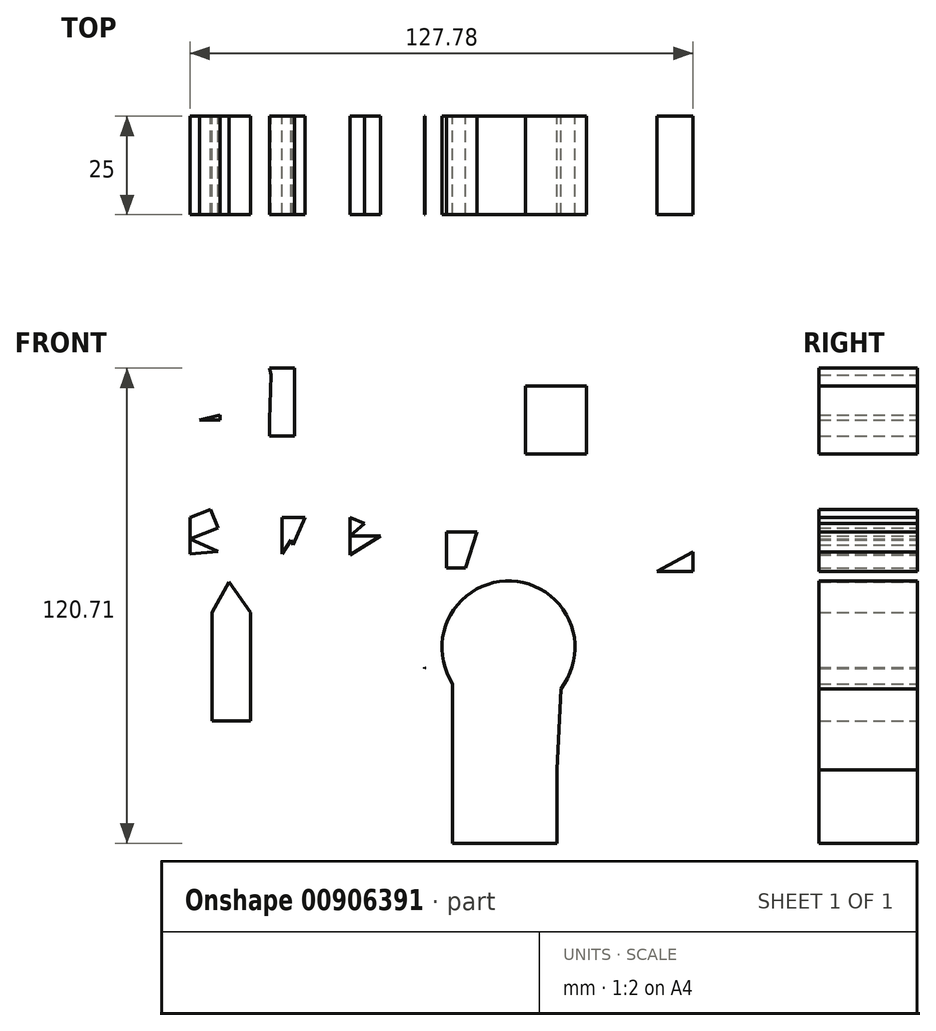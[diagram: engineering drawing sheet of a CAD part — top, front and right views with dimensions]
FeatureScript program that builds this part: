
annotation { "Feature Type Name" : "Feature", "Feature Type Description" : "" }
export const myFeature = defineFeature(function(context is Context, id is Id, definition is map)
    precondition{}
    {
        {
            var Q0;
            Q0=qCreatedBy(makeId("Front.planeOp"),FACE);
            var sketch = newSketch(context, id + "F0", { "sketchPlane" : qUnion([Q0])});
            skArc(sketch, "E0.cCircle", {"start": v(18.84, 36.8) * mm, "mid": v(19.66, -22.39) * mm, "end": v(22.97, 36.71) * mm, "construction": true});
            skLineSegment(sketch, "E0.0", {"start": v(-6.12, 20.79) * mm, "end": v(-3.98, 24.33) * mm});
            skLineSegment(sketch, "E0.1", {"start": v(-3.98, 24.33) * mm, "end": v(-1.36, 27.54) * mm});
            skLineSegment(sketch, "E0.2", {"start": v(-1.36, 27.54) * mm, "end": v(1.68, 30.35) * mm});
            skLineSegment(sketch, "E0.3", {"start": v(1.68, 30.35) * mm, "end": v(5.08, 32.72) * mm});
            skLineSegment(sketch, "E0.4", {"start": v(5.08, 32.72) * mm, "end": v(8.78, 34.59) * mm});
            skLineSegment(sketch, "E0.5", {"start": v(8.78, 34.59) * mm, "end": v(12.7, 35.92) * mm});
            skLineSegment(sketch, "E0.6", {"start": v(12.7, 35.92) * mm, "end": v(16.77, 36.7) * mm});
            skLineSegment(sketch, "E0.7", {"start": v(16.77, 36.7) * mm, "end": v(18.84, 36.8) * mm});
            skLineSegment(sketch, "E0.8", {"start": v(22.97, 36.71) * mm, "end": v(25.03, 36.52) * mm});
            skLineSegment(sketch, "E0.9", {"start": v(25.03, 36.52) * mm, "end": v(29.06, 35.58) * mm});
            skLineSegment(sketch, "E0.10", {"start": v(29.06, 35.58) * mm, "end": v(32.92, 34.08) * mm});
            skLineSegment(sketch, "E0.11", {"start": v(32.92, 34.08) * mm, "end": v(36.54, 32.06) * mm});
            skLineSegment(sketch, "E0.12", {"start": v(36.54, 32.06) * mm, "end": v(39.84, 29.56) * mm});
            skLineSegment(sketch, "E0.13", {"start": v(39.84, 29.56) * mm, "end": v(42.75, 26.62) * mm});
            skLineSegment(sketch, "E0.14", {"start": v(42.75, 26.62) * mm, "end": v(45.24, 23.3) * mm});
            skLineSegment(sketch, "E0.15", {"start": v(45.24, 23.3) * mm, "end": v(47.23, 19.67) * mm});
            skLineSegment(sketch, "E0.16", {"start": v(47.23, 19.67) * mm, "end": v(48.7, 15.8) * mm});
            skLineSegment(sketch, "E0.17", {"start": v(48.7, 15.8) * mm, "end": v(49.62, 11.76) * mm});
            skLineSegment(sketch, "E0.18", {"start": v(49.62, 11.76) * mm, "end": v(49.97, 7.63) * mm});
            skLineSegment(sketch, "E0.19", {"start": v(49.97, 7.63) * mm, "end": v(49.73, 3.5) * mm});
            skLineSegment(sketch, "E0.20", {"start": v(49.73, 3.5) * mm, "end": v(48.93, -0.56) * mm});
            skLineSegment(sketch, "E0.21", {"start": v(48.93, -0.56) * mm, "end": v(47.57, -4.48) * mm});
            skLineSegment(sketch, "E0.22", {"start": v(47.57, -4.48) * mm, "end": v(45.67, -8.16) * mm});
            skLineSegment(sketch, "E0.23", {"start": v(45.67, -8.16) * mm, "end": v(43.29, -11.54) * mm});
            skLineSegment(sketch, "E0.24", {"start": v(43.29, -11.54) * mm, "end": v(40.45, -14.56) * mm});
            skLineSegment(sketch, "E0.25", {"start": v(40.45, -14.56) * mm, "end": v(37.22, -17.16) * mm});
            skLineSegment(sketch, "E0.26", {"start": v(37.22, -17.16) * mm, "end": v(33.67, -19.28) * mm});
            skLineSegment(sketch, "E0.27", {"start": v(33.67, -19.28) * mm, "end": v(29.85, -20.88) * mm});
            skLineSegment(sketch, "E0.28", {"start": v(29.85, -20.88) * mm, "end": v(25.84, -21.94) * mm});
            skLineSegment(sketch, "E0.29", {"start": v(25.84, -21.94) * mm, "end": v(21.73, -22.43) * mm});
            skLineSegment(sketch, "E0.30", {"start": v(21.73, -22.43) * mm, "end": v(17.6, -22.35) * mm});
            skLineSegment(sketch, "E0.31", {"start": v(17.6, -22.35) * mm, "end": v(13.5, -21.68) * mm});
            skLineSegment(sketch, "E0.32", {"start": v(13.5, -21.68) * mm, "end": v(9.55, -20.46) * mm});
            skLineSegment(sketch, "E0.33", {"start": v(9.55, -20.46) * mm, "end": v(5.8, -18.7) * mm});
            skLineSegment(sketch, "E0.34", {"start": v(5.8, -18.7) * mm, "end": v(2.33, -16.43) * mm});
            skLineSegment(sketch, "E0.35", {"start": v(2.33, -16.43) * mm, "end": v(-0.78, -13.7) * mm});
            skLineSegment(sketch, "E0.36", {"start": v(-0.78, -13.7) * mm, "end": v(-3.49, -10.56) * mm});
            skLineSegment(sketch, "E0.37", {"start": v(-3.49, -10.56) * mm, "end": v(-5.73, -7.08) * mm});
            skLineSegment(sketch, "E0.38", {"start": v(-5.73, -7.08) * mm, "end": v(-7.47, -3.32) * mm});
            skLineSegment(sketch, "E0.39", {"start": v(-7.47, -3.32) * mm, "end": v(-8.67, 0.64) * mm});
            skLineSegment(sketch, "E0.40", {"start": v(-8.67, 0.64) * mm, "end": v(-9.3, 4.73) * mm});
            skLineSegment(sketch, "E0.41", {"start": v(-9.3, 4.73) * mm, "end": v(-9.36, 8.88) * mm});
            skLineSegment(sketch, "E0.42", {"start": v(-9.36, 8.88) * mm, "end": v(-8.84, 12.99) * mm});
            skLineSegment(sketch, "E0.43", {"start": v(-8.84, 12.99) * mm, "end": v(-7.75, 16.98) * mm});
            skLineSegment(sketch, "E0.44", {"start": v(-7.75, 16.98) * mm, "end": v(-6.12, 20.79) * mm});
            skPoint(sketch, "E0.0.midPoint", {"position": v(-5.05, 22.56) * mm});
            skLineSegment(sketch, "E1", {"start": v(2.33, -16.43) * mm, "end": v(2.33, -16.7) * mm});
            skLineSegment(sketch, "E2", {"start": v(2.33, -16.7) * mm, "end": v(2.58, -16.52) * mm});
            skLineSegment(sketch, "E3", {"start": v(25.44, 0) * mm, "end": v(11.35, 0) * mm});
            skLineSegment(sketch, "E4", {"start": v(7.9, 8.88) * mm, "end": v(7.9, 17.96) * mm});
            skLineSegment(sketch, "E5", {"start": v(7.9, 17.96) * mm, "end": v(15.66, 17.96) * mm});
            skLineSegment(sketch, "E6", {"start": v(15.66, 17.96) * mm, "end": v(12.79, 8.88) * mm});
            skLineSegment(sketch, "E7", {"start": v(12.79, 8.88) * mm, "end": v(7.9, 8.88) * mm});
            skLineSegment(sketch, "E8", {"start": v(28.3, 17.96) * mm, "end": v(28.3, 6.47) * mm});
            skLineSegment(sketch, "E9", {"start": v(28.88, 6.47) * mm, "end": v(39.23, 6.47) * mm});
            skLineSegment(sketch, "E10", {"start": v(39.23, 6.47) * mm, "end": v(39.23, 17.96) * mm});
            skLineSegment(sketch, "E11", {"start": v(38.66, 19.4) * mm, "end": v(28.3, 17.96) * mm});
            skLineSegment(sketch, "E12", {"start": v(9.55, -20.46) * mm, "end": v(9.55, -42.4) * mm});
            skLineSegment(sketch, "E13", {"start": v(9.55, -42.4) * mm, "end": v(36.07, -42.4) * mm});
            skLineSegment(sketch, "E14", {"start": v(36.07, -42.4) * mm, "end": v(37.22, -17.16) * mm});
            skLineSegment(sketch, "E15", {"start": v(36.65, -29.78) * mm, "end": v(47.53, -33.15) * mm});
            skLineSegment(sketch, "E16", {"start": v(9.55, -31.43) * mm, "end": v(-4.45, -42.4) * mm});
            skLineSegment(sketch, "E17", {"start": v(9.55, -42.4) * mm, "end": v(9.55, -61.07) * mm});
            skLineSegment(sketch, "E18", {"start": v(9.55, -61.07) * mm, "end": v(36.07, -61.07) * mm});
            skLineSegment(sketch, "E19", {"start": v(36.07, -61.07) * mm, "end": v(36.07, -42.4) * mm});
            skLineSegment(sketch, "E20", {"start": v(15.66, -61.07) * mm, "end": v(15.66, -77.46) * mm});
            skLineSegment(sketch, "E21", {"start": v(30.32, -61.07) * mm, "end": v(30.32, -77.74) * mm});
            skLineSegment(sketch, "E22", {"start": v(-6.12, 23.71) * mm, "end": v(-14.89, 24.11) * mm});
            skLineSegment(sketch, "E23", {"start": v(-9.34, 30.6) * mm, "end": v(-1.36, 27.54) * mm});
            skLineSegment(sketch, "E24", {"start": v(-1.36, 36.07) * mm, "end": v(1.68, 30.35) * mm});
            skLineSegment(sketch, "E25", {"start": v(9.55, 40.96) * mm, "end": v(12.7, 35.92) * mm});
            skLineSegment(sketch, "E26", {"start": v(1.68, 40.1) * mm, "end": v(8.78, 34.59) * mm});
            skLineSegment(sketch, "E27", {"start": v(15.66, 43.83) * mm, "end": v(16.77, 36.7) * mm});
            skLineSegment(sketch, "E28", {"start": v(32.33, 44.7) * mm, "end": v(25.03, 36.52) * mm});
            skLineSegment(sketch, "E29", {"start": v(36.07, 42.1) * mm, "end": v(29.06, 35.58) * mm});
            skLineSegment(sketch, "E30", {"start": v(45.24, 23.3) * mm, "end": v(54.67, 30.35) * mm});
            skLineSegment(sketch, "E31", {"start": v(42.75, 26.62) * mm, "end": v(47.23, 38.26) * mm});
            skLineSegment(sketch, "E32", {"start": v(47.23, 19.67) * mm, "end": v(58.6, 25.92) * mm});
            skPoint(sketch, "E33.end.orphan", {"position": v(39.8, 42.1) * mm});
            skPoint(sketch, "E33.start.orphan", {"position": v(39.8, 35.58) * mm});
            skLineSegment(sketch, "E34", {"start": v(39.8, 35.58) * mm, "end": v(36.54, 32.06) * mm});
            skPoint(sketch, "E35.orphan", {"position": v(81.48, -49.87) * mm});
            skLineSegment(sketch, "E36", {"start": v(15.1, -42.4) * mm, "end": v(22.8, -42.4) * mm});
            skPoint(sketch, "E37.start.orphan", {"position": v(58.49, -49.87) * mm});
            skLineSegment(sketch, "E38", {"start": v(-47.28, -30.03) * mm, "end": v(-47.28, -59.06) * mm});
            skLineSegment(sketch, "E39", {"start": v(-47.28, -30.03) * mm, "end": v(-51.59, -30.03) * mm});
            skLineSegment(sketch, "E40", {"start": v(-47.28, -30.03) * mm, "end": v(-41.82, -30.03) * mm});
            skLineSegment(sketch, "E41", {"start": v(-41.82, -30.03) * mm, "end": v(-41.82, -2.44) * mm});
            skLineSegment(sketch, "E42", {"start": v(-41.82, -2.44) * mm, "end": v(-51.59, -2.44) * mm});
            skLineSegment(sketch, "E43", {"start": v(-51.59, -2.44) * mm, "end": v(-51.59, -30.03) * mm});
            skLineSegment(sketch, "E44", {"start": v(-51.59, -2.44) * mm, "end": v(-47.28, 5.32) * mm});
            skLineSegment(sketch, "E45", {"start": v(-47.28, 5.32) * mm, "end": v(-41.82, -2.44) * mm});
            skLineSegment(sketch, "E46", {"start": v(-44.55, -30.03) * mm, "end": v(-41.82, -36.64) * mm});
            skPoint(sketch, "E47.start.orphan", {"position": v(12.79, -49.87) * mm});
            skPoint(sketch, "E48.end.orphan", {"position": v(15.66, -49.87) * mm});
            skPoint(sketch, "E49.start.orphan", {"position": v(20.84, -49.87) * mm});
            skPoint(sketch, "E50.end.orphan", {"position": v(29.17, -42.4) * mm});
            skLineSegment(sketch, "E51", {"start": v(-47.28, 57.05) * mm, "end": v(-54.75, 57.05) * mm});
            skLineSegment(sketch, "E52", {"start": v(-54.75, 57.05) * mm, "end": v(-54.75, 51.02) * mm});
            skLineSegment(sketch, "E53", {"start": v(-54.75, 51.02) * mm, "end": v(-49.58, 51.02) * mm});
            skLineSegment(sketch, "E54", {"start": v(-49.58, 51.02) * mm, "end": v(-49.58, 46.42) * mm});
            skLineSegment(sketch, "E55", {"start": v(-49.58, 46.42) * mm, "end": v(-54.75, 46.42) * mm});
            skLineSegment(sketch, "E56", {"start": v(-54.75, 46.42) * mm, "end": v(-49.58, 47.75) * mm});
            skLineSegment(sketch, "E57", {"start": v(-36.93, 51.02) * mm, "end": v(-36.93, 42.4) * mm});
            skLineSegment(sketch, "E58", {"start": v(-36.93, 42.4) * mm, "end": v(-30.6, 42.4) * mm});
            skLineSegment(sketch, "E59", {"start": v(-30.6, 42.4) * mm, "end": v(-30.6, 59.64) * mm});
            skLineSegment(sketch, "E60", {"start": v(-30.6, 59.64) * mm, "end": v(-36.93, 59.64) * mm});
            skLineSegment(sketch, "E61", {"start": v(-36.93, 59.64) * mm, "end": v(-36.64, 57.91) * mm});
            skLineSegment(sketch, "E62", {"start": v(-36.64, 57.91) * mm, "end": v(-36.93, 46.42) * mm});
            skLineSegment(sketch, "E63", {"start": v(-19.1, 45.97) * mm, "end": v(-19.1, 59.64) * mm});
            skLineSegment(sketch, "E64", {"start": v(4.17, 59.64) * mm, "end": v(4.17, 50.15) * mm});
            skLineSegment(sketch, "E65", {"start": v(4.17, 50.15) * mm, "end": v(9.34, 50.15) * mm});
            skLineSegment(sketch, "E66", {"start": v(9.34, 50.73) * mm, "end": v(9.34, 58.78) * mm});
            skLineSegment(sketch, "E67", {"start": v(16.53, 58.78) * mm, "end": v(16.53, 50.15) * mm});
            skLineSegment(sketch, "E68", {"start": v(15.95, 49.3) * mm, "end": v(23.14, 58.78) * mm});
            skLineSegment(sketch, "E69", {"start": v(23.14, 57.34) * mm, "end": v(23.14, 50.15) * mm});
            skLineSegment(sketch, "E70", {"start": v(35.5, 58.78) * mm, "end": v(31.76, 50.15) * mm});
            skLineSegment(sketch, "E71", {"start": v(35.5, 58.78) * mm, "end": v(38.94, 50.15) * mm});
            skLineSegment(sketch, "E72", {"start": v(35.5, 54.46) * mm, "end": v(31.76, 50.15) * mm});
            skPoint(sketch, "E72.startSnap0", {"position": v(37.22, 54.46) * mm});
            skLineSegment(sketch, "E73", {"start": v(-65.67, 21.7) * mm, "end": v(-69.32, 13.28) * mm});
            skLineSegment(sketch, "E74", {"start": v(-65.67, 21.7) * mm, "end": v(-62.34, 13.37) * mm});
            skLineSegment(sketch, "E75", {"start": v(-67.4, 16.81) * mm, "end": v(-62.34, 14.62) * mm});
            skLineSegment(sketch, "E76", {"start": v(-62.34, 14.62) * mm, "end": v(-57.19, 12.39) * mm});
            skLineSegment(sketch, "E77", {"start": v(-57.19, 12.39) * mm, "end": v(-57.19, 21.7) * mm});
            skLineSegment(sketch, "E78", {"start": v(-57.19, 21.7) * mm, "end": v(-52.01, 23.77) * mm});
            skLineSegment(sketch, "E79", {"start": v(-52.01, 23.77) * mm, "end": v(-50.11, 19.01) * mm});
            skLineSegment(sketch, "E80", {"start": v(-50.11, 19.01) * mm, "end": v(-57.19, 16.18) * mm});
            skLineSegment(sketch, "E81", {"start": v(-57.19, 16.18) * mm, "end": v(-50.11, 13.12) * mm});
            skLineSegment(sketch, "E82", {"start": v(-50.11, 13.12) * mm, "end": v(-57.19, 12.39) * mm});
            skLineSegment(sketch, "E83", {"start": v(-40.1, 21.7) * mm, "end": v(-40.1, 12.39) * mm});
            skLineSegment(sketch, "E84", {"start": v(-33.77, 21.7) * mm, "end": v(-30.05, 12.39) * mm});
            skLineSegment(sketch, "E85", {"start": v(-32.05, 12.21) * mm, "end": v(-27.94, 21.7) * mm});
            skLineSegment(sketch, "E86", {"start": v(-27.94, 21.7) * mm, "end": v(-33.77, 12.39) * mm});
            skLineSegment(sketch, "E87", {"start": v(-33.77, 12.39) * mm, "end": v(-33.77, 21.7) * mm});
            skLineSegment(sketch, "E88", {"start": v(-33.77, 21.7) * mm, "end": v(-27.94, 21.7) * mm});
            skLineSegment(sketch, "E89", {"start": v(-27.94, 21.7) * mm, "end": v(-27.94, 12.21) * mm});
            skLineSegment(sketch, "E90", {"start": v(-24.57, 21.7) * mm, "end": v(-24.57, 12.21) * mm});
            skLineSegment(sketch, "E91", {"start": v(-24.57, 21.7) * mm, "end": v(-20.78, 12.21) * mm});
            skLineSegment(sketch, "E92", {"start": v(-20.84, 13.36) * mm, "end": v(-20.84, 23.77) * mm});
            skLineSegment(sketch, "E93", {"start": v(-16.53, 21.7) * mm, "end": v(-16.53, 12.21) * mm});
            skLineSegment(sketch, "E94", {"start": v(-16.53, 21.7) * mm, "end": v(-12.89, 20.12) * mm});
            skLineSegment(sketch, "E95", {"start": v(-12.89, 20.12) * mm, "end": v(-16.53, 16.96) * mm});
            skLineSegment(sketch, "E96", {"start": v(-16.53, 16.96) * mm, "end": v(-8.84, 16.98) * mm});
            skLineSegment(sketch, "E97", {"start": v(-8.84, 16.98) * mm, "end": v(-16.53, 12.21) * mm});
            skLineSegment(sketch, "E98", {"start": v(-16.24, 13.08) * mm, "end": v(-8.77, 12.94) * mm});
            skLineSegment(sketch, "E99", {"start": v(56.48, 11.76) * mm, "end": v(53.4, 4.67) * mm});
            skLineSegment(sketch, "E100", {"start": v(53.4, 4.67) * mm, "end": v(58.74, 16.98) * mm});
            skLineSegment(sketch, "E101", {"start": v(58.74, 16.98) * mm, "end": v(53.16, 19.4) * mm});
            skLineSegment(sketch, "E102", {"start": v(53.16, 19.4) * mm, "end": v(61.36, 16.98) * mm});
            skLineSegment(sketch, "E103", {"start": v(70.59, 12.99) * mm, "end": v(61.41, 7.94) * mm});
            skLineSegment(sketch, "E104", {"start": v(61.41, 7.94) * mm, "end": v(70.59, 7.94) * mm});
            skLineSegment(sketch, "E105", {"start": v(70.59, 7.94) * mm, "end": v(70.59, 12.99) * mm});
            skLineSegment(sketch, "E106.trimOffspring", {"start": v(28.3, 12.27) * mm, "end": v(39.23, 12.07) * mm});
            skLineSegment(sketch, "E107.trimOffspring", {"start": v(7.9, 12.64) * mm, "end": v(13.95, 12.53) * mm});
            skLineSegment(sketch, "E108.trimOffspring", {"start": v(49.53, 11.89) * mm, "end": v(56.48, 11.76) * mm});
            skPoint(sketch, "E109.end.orphan", {"position": v(43.26, 42.1) * mm});
            skPoint(sketch, "E110.orphan", {"position": v(20.9, 36.9) * mm});
            skSolve(sketch);
        }
        {
            var Q0;
            Q0 = qSketchRegion(id + "F0", true);
            extrude(context, id + "F1", {"entities" : qUnion([Q0]), "depth" : 25 * mm, "offsetDistance" : 25 * mm});
        }
        {
            var Q0;
            Q0=qCreatedBy(makeId("Front.planeOp"),FACE);
            var sketch = newSketch(context, id + "F2", { "sketchPlane" : qUnion([Q0])});
            skLineSegment(sketch, "E111.bottom", {"start": v(43.54, 37.8) * mm, "end": v(28.02, 37.8) * mm});
            skLineSegment(sketch, "E111.top", {"start": v(43.54, 55.04) * mm, "end": v(28.02, 55.04) * mm});
            skLineSegment(sketch, "E111.left", {"start": v(43.54, 37.8) * mm, "end": v(43.54, 55.04) * mm});
            skLineSegment(sketch, "E111.right", {"start": v(28.02, 37.8) * mm, "end": v(28.02, 55.04) * mm});
            skSolve(sketch);
        }
        {
            var Q0;
            Q0=makeQuery(id+"F2.imprint","IMPRINT",FACE,{"disambiguationData":[TD([[makeQuery(id+"F2.imprint","IMPRINT",EDGE,{"derivedFrom":sQuery(id+"F2.wireOp",EDGE,"E111.bottom")}),-1.0]])]});
            extrude(context, id + "F3", {"entities" : qUnion([Q0]), "depth" : 25 * mm, "offsetDistance" : 25 * mm});
        }
        {
            var Q0;
            Q0=qCreatedBy(makeId("Front.planeOp"),FACE);
            var sketch = newSketch(context, id + "F4", { "sketchPlane" : qUnion([Q0])});
            skCircle(sketch, "E112", {"center": v(23.71, -11.35) * mm, "radius": 16.92 * mm});
            skSolve(sketch);
        }
        {
            var Q0;
            Q0 = qSketchRegion(id + "F4", true);
            extrude(context, id + "F5", {"entities" : qUnion([Q0]), "operationType" : NewBodyOperationType.ADD, "depth" : 25 * mm, "offsetDistance" : 25 * mm});
        }
    });
